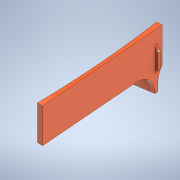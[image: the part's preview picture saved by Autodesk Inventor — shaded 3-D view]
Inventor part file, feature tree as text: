
AUTODESK INVENTOR PART (.ipt)
format: ipt  version: 2020.3 (Build 243373000, 373)  size: 211,968 bytes
history: native  units: mm
features: other x7, extrude x6, sketch x6, fillet x5, reference x5, plane x1, projected_geometry x1
ambient origin geometry x8: Origin, YZ Plane, XZ Plane, XY Plane, X Axis, Y Axis, Z Axis, Center Point
bodies: Solid1 (feature_tree)
feature tree (31):
  other  "Blocks"
  extrude  "Extrusion1"  Depth=5.0mm
  extrude  "Extrusion2"  Depth=2.5mm
  extrude  "Extrusion3"  Depth=5.0mm
  fillet  "Fillet1"  Radius=2.5mm
  fillet  "Fillet2"  Radius=5.0mm
  fillet  "Fillet3"  Radius=20.0mm
  fillet  "Fillet4"  Radius=3.25mm
  sketch  "Sketch4"  dims[d14=20.0mm d15=20.0mm]
  plane  "Work Plane1"
  extrude  "Extrusion4"  Depth=20.0mm
  extrude  "Extrusion5"  Depth=1.5mm TaperAngle=0.0deg
  extrude  "Extrusion6"  Depth=10.0mm TaperAngle=0.0deg
  fillet  "Fillet5"  Radius=1.75mm
  sketch  "Sketch1"  dims[d1=5.0mm d2=5.0mm]
  other  "Arc"
  sketch  "Sketch2"  dims[d3=33.0mm d4=0.0mm d5=2.5mm]
  sketch  "Sketch3"  dims[d6=15.0mm d7=5.0mm d8=2.5mm d9=0.0mm d10=5.0mm d11=20.0mm d12=0.0mm d13=3.25mm]
  reference  "Reference1"
  reference  "Reference2"
  sketch  "Sketch5"  dims[d16=7.25mm d17=1.5mm d18=0.0mm]
  reference  "Reference3"
  reference  "Reference4"
  reference  "Reference5"
  sketch  "Sketch6"  dims[d19=10.0mm d20=0.0mm d21=10.0mm d22=0.0mm d23=1.75mm]
  projected_geometry  "Projected Loop1"
  other  "Arc:1"
  other  "<userpath>\Documents\Inventor\TheArch\R&D\Beta0\Structura\Prototip\Prototip1.iam"
  other  "Prototip1.iam"
  other  "MG996:3"
  other  "PrindereDisc:1"
